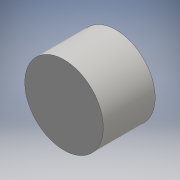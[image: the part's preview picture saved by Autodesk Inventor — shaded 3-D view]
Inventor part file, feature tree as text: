
AUTODESK INVENTOR PART (.ipt)
format: ipt  version: 2016 (Build 200138000, 138)  size: 88,064 bytes
history: native  units: mm
features: other x1, extrude x1, sketch x1
ambient origin geometry x8: Origin, YZ Plane, XZ Plane, XY Plane, X Axis, Y Axis, Z Axis, Center Point
bodies: Body1 (feature_tree)
feature tree (3):
  other  "ソリッド1"
  extrude  "押し出し1"  Depth=32.5mm
  sketch  "スケッチ1"
